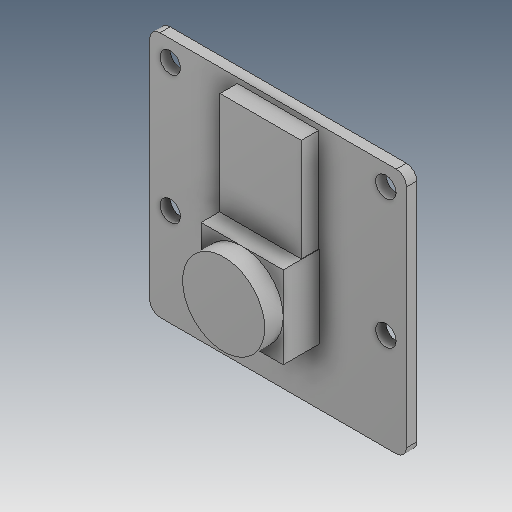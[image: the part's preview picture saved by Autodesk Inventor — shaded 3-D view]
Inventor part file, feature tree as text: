
AUTODESK INVENTOR PART (.ipt)
format: ipt  version: 2020 (Build 240168000, 168)  size: 178,176 bytes
history: mixed  units: mm
features: extrude x3, sketch x3, other x1, imported_body x1
ambient origin geometry x8: Origin, YZ Plane, XZ Plane, XY Plane, X Axis, Y Axis, Z Axis, Center Point
bodies: Solid1 (imported_parasolid)
feature tree (8):
  extrude  "Extrusion1"  Depth=3.0mm TaperAngle=0.0deg
  extrude  "Extrusion3"  [1 undecoded]
  extrude  "Extrusion4"  [1 undecoded]
  sketch  "Sketch1"  dims[d0=19.0mm d1=0.0mm d4=3.0mm d5=0.0mm]
  sketch  "Sketch3"  dims[d6=22.0mm d7=0.0mm]
  sketch  "Sketch4"
  other  "Boss-Extrude1"
  imported_body  NMx_Import_Brep_tag  [imported B-rep: ~28 faces, bbox_mm=[25.0, 24.0, 6.3]]
note: 2 required parameter values undecoded (feature->parameter linkage not recoverable at this tier; creation-order binding heuristic only, values carry confidence <= 0.55)
